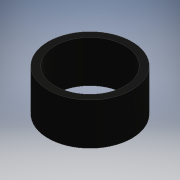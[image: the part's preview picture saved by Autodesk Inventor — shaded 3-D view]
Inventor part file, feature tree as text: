
AUTODESK INVENTOR PART (.ipt)
format: ipt  version: 2020.2 (Build 242310000, 310)  size: 93,696 bytes
history: native  units: mm
features: other x1, extrude x1, sketch x1
ambient origin geometry x8: Origin, YZ Plane, XZ Plane, XY Plane, X Axis, Y Axis, Z Axis, Center Point
bodies: Body1 (feature_tree)
feature tree (3):
  other  "ソリッド1"
  extrude  "押し出し1"  Depth=12.0mm
  sketch  "スケッチ1"
